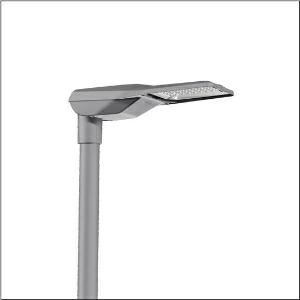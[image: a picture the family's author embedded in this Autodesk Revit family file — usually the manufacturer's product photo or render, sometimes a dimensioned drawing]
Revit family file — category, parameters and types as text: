
# Revit family: streetlight_sl_21_iq_mini___pl52_5xe2h31d08gb_8f57
name_source: partatom
category: Lighting Fixtures
units: mm (PartAtom-declared; Revit-internal decimal feet)

## family parameters
Cut with Voids When Loaded = No
Host = Face
Light Source = No
Part Type = Normal
Room Calculation Point = No
Round Connector Dimension = Use Diameter
Shared = No

## types (1)
- --- (1 x LED, 5580 lm, 37.1 W, 3000K)
    Apparent Load = 37 VA
    CIE Flux Codes = 27 59 98 100 100
    Color Rendering = 70
    Color Temperature = 3000K
    Default Elevation = 1800 mm
    Description = Streetlight SL 21 iQ mini, mast luminaire, primary light control with lens, of PMMA, primary optical cover: cover, of toughened safety glass, transparent, light distribution: PL52, light emission: direct distribution, primary light characteristic: asymmetric, installation type: post-top, side-entry, LED, High Power LED, rated luminous flux: 5.580lm, luminous efficacy: 150lm/W, light colour: 730, colour temperature: 3000K, control: Auto-Match, Temp-Guard, Lumen-Switch, Night-Set, Smart-Wire, Light-Fading, Desk-Remote (wireless, voltage-free reading and setting of iQ features in the workshop via application-optimized NFC function/RFID function), optimised constant luminous flux control (CLO 2.0), presetting dimming linear, mains connection: 220..240V, AC, 50/60Hz, start of lifetime: 37W, end of service life: 39W, reduction: 18W, luminaire housing, of diecast aluminium, powder-coated, Siteco® metallic grey (DB 702S), corrosivity category C5 mid according to DIN EN ISO 12944, please order mast flange separately, inclination adjustable: 0°, 5°, 10°, 15°, sealing non-destructively replaceable, multi-level sealing system, length: 628mm, width: 235mm, height: 110mm, mast flange for spigot size: 42mm (side-entry): 5XC10008XM4, 60/48mm (side-entry/post-top): 5XC10108XM2, 76/60mm (side-entry/post-top): 5XC10108XM1, protection rating (complete): IP66, insulation class (complete): insulation class II (safety insulation), certification: CE, ENEC, ENEC+, VDE, impact resistance: IK09, permissible operating ambient temperature for outdoor applications: -40..+50°C, standard-compliant lighting for roads and squares, packaging unit: 1 piece

Light Distribution: PL52
    Height = 110 mm
    Lamp = 1 x LED
    Lamp Light Flux = 5580 lm
    Lamp Power = 37.1 W
    Lamp count = 1
    Length = 625 mm
    Luminous efficacy = 150 lm/W
    Manufacturer = Siteco
    ModVariant = No
    Model = 5XE2H31D08GB
    Number of Poles = 1
    OnlyDefault = Yes
    Power Factor = 1
    Product Name = Streetlight SL 21 iQ mini | PL52
    Product group = mast luminaire | pylon top
    ProductGroupID = 6100
    Protection Class = Protection class II
    Protection Degree = IP 66
    RLX_Detail_Level = 1
    RLX_Emergency_Light_Flux = 0 lm
    RLX_Emergency_Type = 0
    RLX_Emergency_Type_DB = No
    RlxData = <blob elided: 101981 chars, md5=5adda6d1>
    Socket = socket
    Standby Power = 0 W
    System Light Flux = 5580 lm
    System Power = 37 W
    Type Comments = factory setting: luminous flux: 100 % | dim-lin: 254 | 385 mA
    Type Image = l_1003519.jpg
    URL = http://relux.com
    VarID = @adj_124349
    Voltage = 0 V
    Weight = 0.00 kg
    Width = 234 mm

## geometry (parser evidence)
native form markers: Blend x4, Sweep x10
no freeform markers — native parametric forms only
